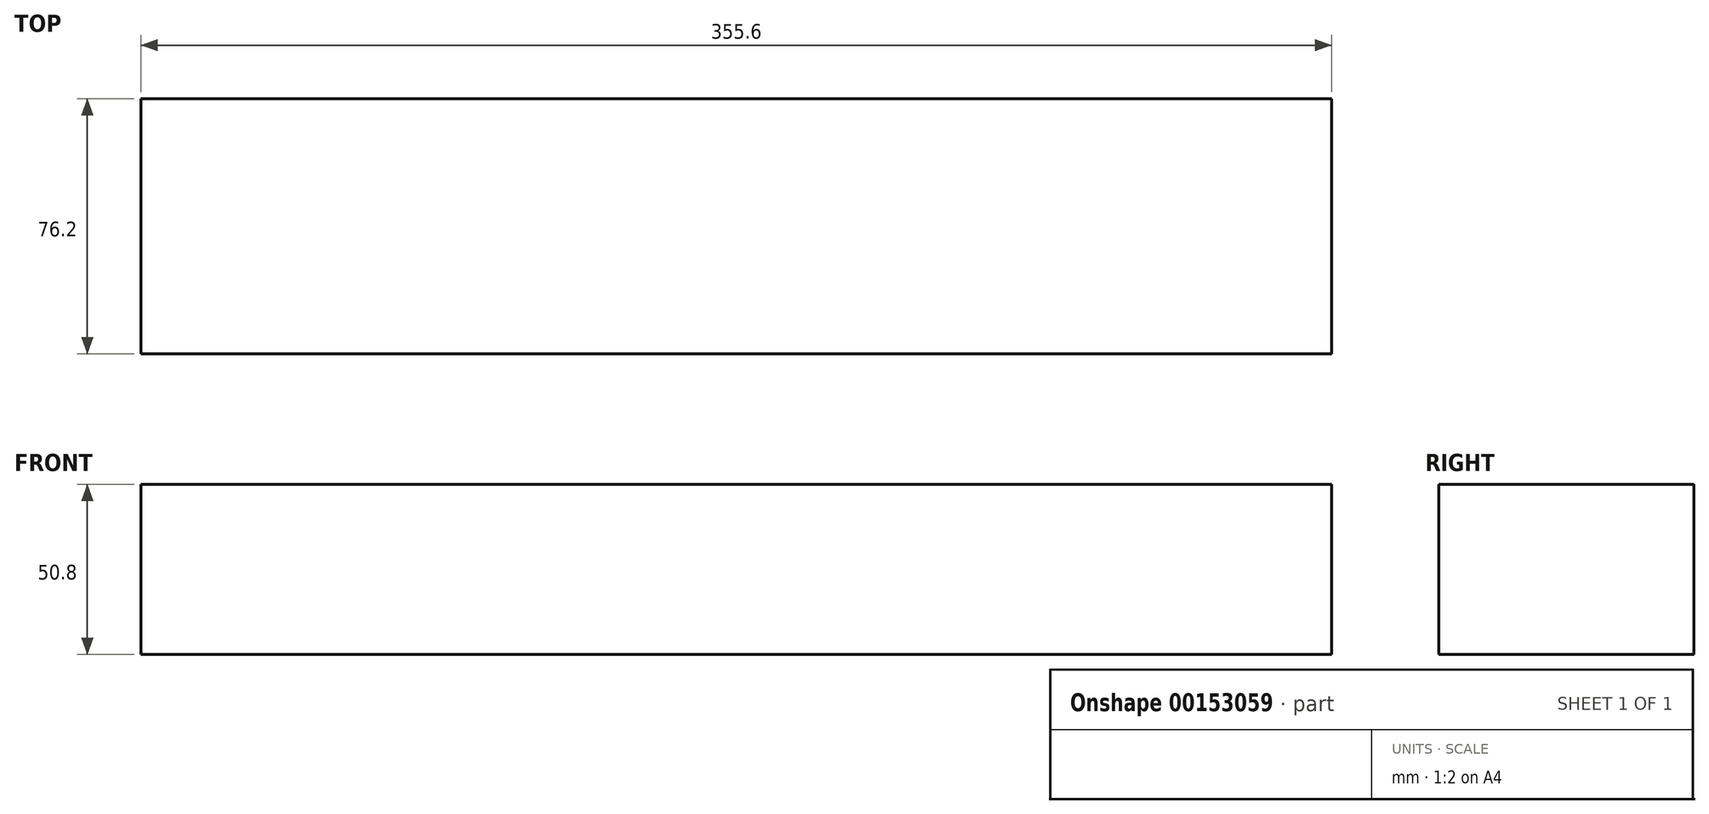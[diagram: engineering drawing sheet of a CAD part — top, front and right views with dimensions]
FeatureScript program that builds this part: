
annotation { "Feature Type Name" : "Feature", "Feature Type Description" : "" }
export const myFeature = defineFeature(function(context is Context, id is Id, definition is map)
    precondition{}
    {
        {
            var Q0;
            Q0=qCreatedBy(makeId("Top.planeOp"),FACE);
            var sketch = newSketch(context, id + "F0", { "sketchPlane" : qUnion([Q0])});
            skLineSegment(sketch, "E0.bottom", {"start": v(0, 0.38) * mm, "end": v(355.6, 0.38) * mm});
            skLineSegment(sketch, "E0.top", {"start": v(0, 76.58) * mm, "end": v(355.6, 76.58) * mm});
            skLineSegment(sketch, "E0.left", {"start": v(0, 0.38) * mm, "end": v(0, 76.58) * mm});
            skLineSegment(sketch, "E0.right", {"start": v(355.6, 0.38) * mm, "end": v(355.6, 76.58) * mm});
            skSolve(sketch);
        }
        {
            var Q0;
            Q0=makeQuery(id+"F0.imprint","IMPRINT",FACE,{"disambiguationData":[TD([[makeQuery(id+"F0.imprint","IMPRINT",EDGE,{"derivedFrom":sQuery(id+"F0.wireOp",EDGE,"E0.bottom")}),1.0]])]});
            extrude(context, id + "F1", {"entities" : qUnion([Q0]), "depth" : 50.8 * mm});
        }
    });
